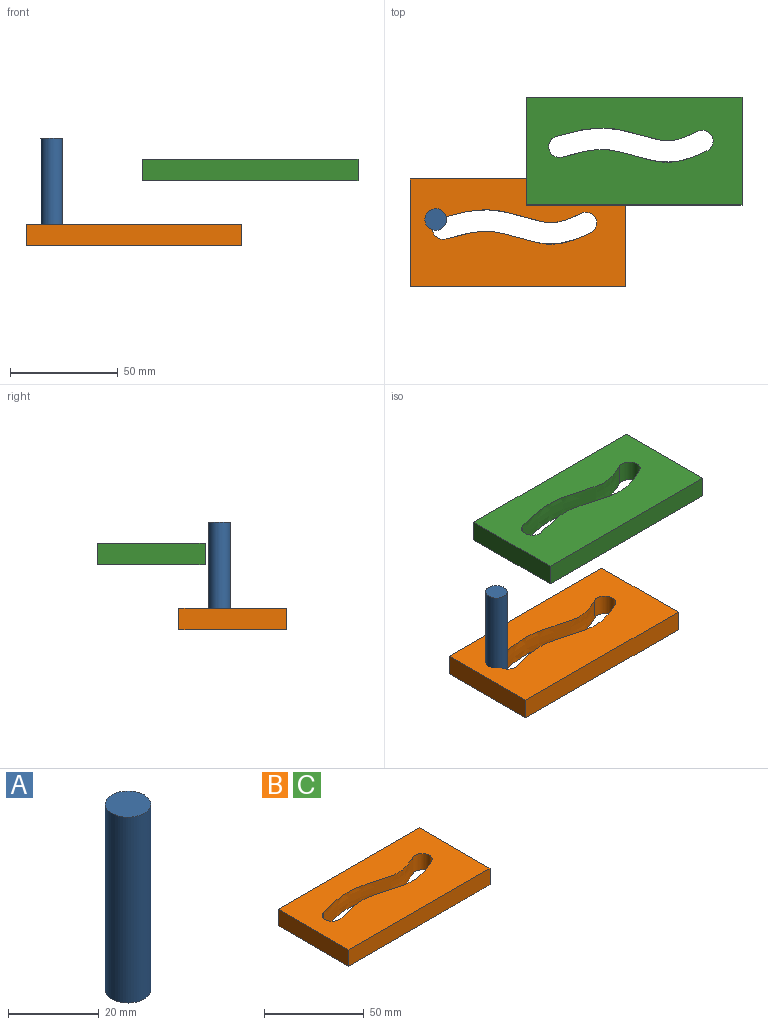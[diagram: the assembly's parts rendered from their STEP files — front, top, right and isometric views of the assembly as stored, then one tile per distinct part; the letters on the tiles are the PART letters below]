
ASSEMBLY  parts=3 mates=1
PART A: 3 faces, bbox 10x10x50 mm
  f0: cylinder r=5mm len=50mm, axis (0,0,-1), area 1570.8mm2, adj f1,f2
  f1: plane 10x10mm, normal (0,0,1), area 78.5mm2, adj f0
  f2: plane 10x10mm, normal (0,0,-1), area 78.5mm2, adj f0
PART B: 10 faces, bbox 100x50x10 mm
  f0: plane 50x10mm, normal (-1,0,0), area 500mm2, adj f1,f3,f4,f5
  f1: plane 100x10mm, normal (0,-1,0), area 1000mm2, adj f0,f2,f4,f5
  f2: plane 50x10mm, normal (1,0,0), area 500mm2, adj f1,f3,f4,f5
  f3: plane 100x10mm, normal (0,1,0), area 1000mm2, adj f0,f2,f4,f5
  f4: plane 100x50mm, normal (0,0,1), area 4239.2mm2, adj f0,f1,f2,f3,f6,f7,f8,f9
  f5: plane 100x50mm, normal (0,0,-1), area 4239.2mm2, adj f0,f1,f2,f3,f6,f7,f8,f9
  f6: extruded ~65.5x10mm, area 673.5mm2, adj f4,f5,f7,f9
  f7: cylinder r=5mm len=10mm, axis (0,0,1), area 157.1mm2, adj f4,f5,f6,f8
  f8: extruded ~67.01x10mm, area 691.1mm2, adj f4,f5,f7,f9
  f9: cylinder r=5mm len=10mm, axis (0,0,1), area 157.1mm2, adj f4,f5,f6,f8
PART C: same geometry as B
PLACE A t=(-6.67,0.26,11.21)mm
PLACE B t=(-3.25,-3.89,11.21)mm fixed
PLACE C t=(50.69,34.02,41.35)mm
MATE planar A.f0 <-> B.f5  axis (0,0,-1) through (-43.31,27.25,11.21)mm
